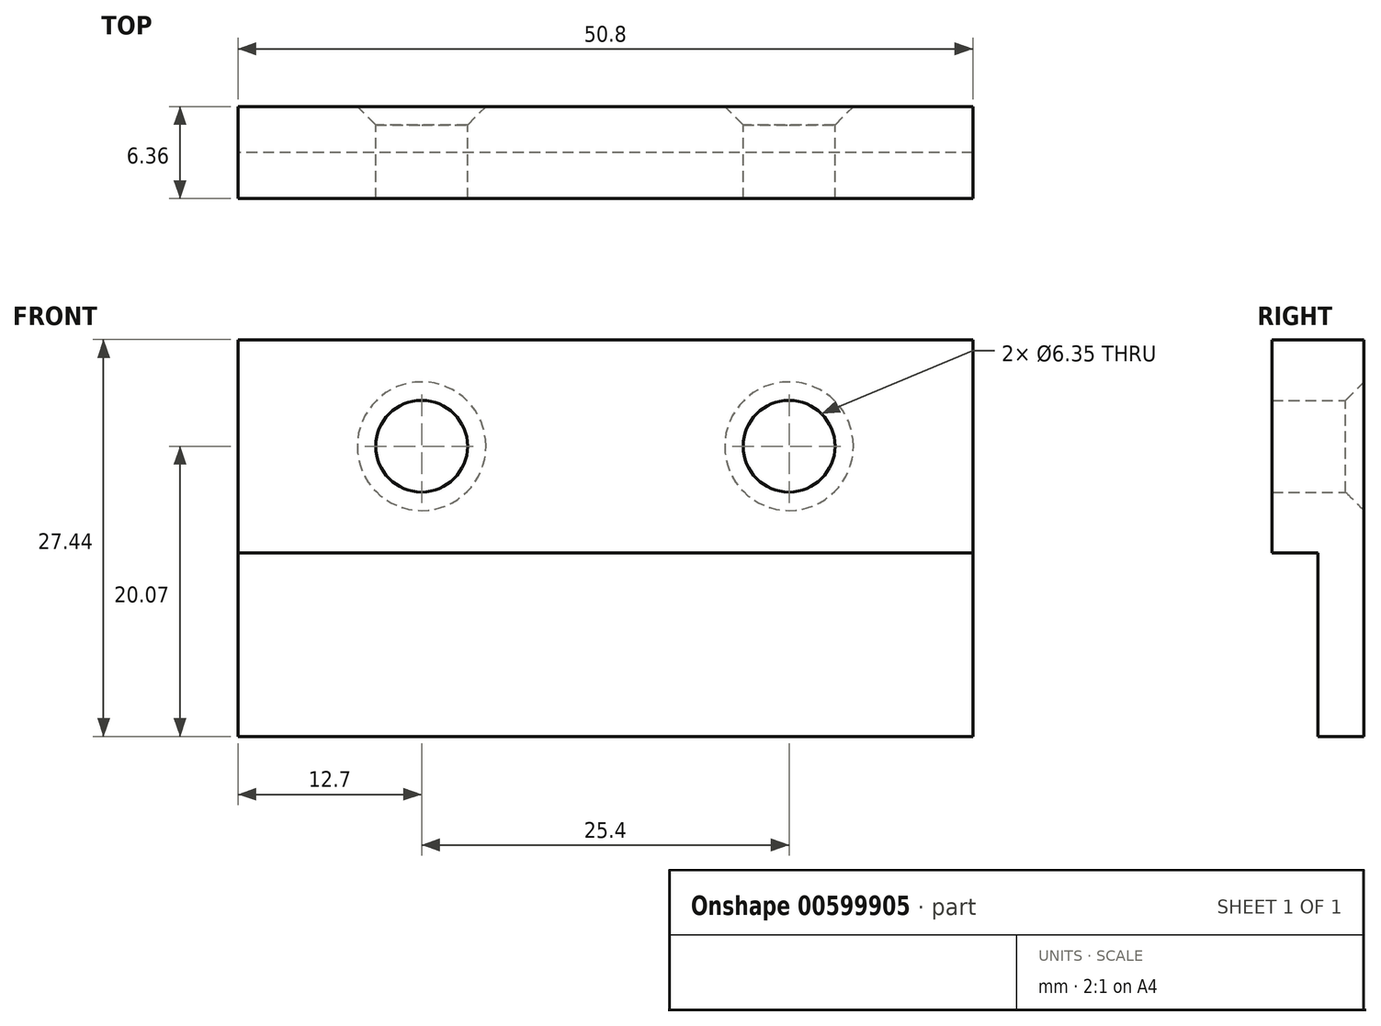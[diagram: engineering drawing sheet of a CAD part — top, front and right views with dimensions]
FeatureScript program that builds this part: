
annotation { "Feature Type Name" : "Feature", "Feature Type Description" : "" }
export const myFeature = defineFeature(function(context is Context, id is Id, definition is map)
    precondition{}
    {
        {
            var Q0;
            Q0=qCreatedBy(makeId("Front.planeOp"),FACE);
            var sketch = newSketch(context, id + "F0", { "sketchPlane" : qUnion([Q0])});
            skLineSegment(sketch, "E0.bottom", {"start": v(25.4, -7.37) * mm, "end": v(-25.4, -7.37) * mm});
            skLineSegment(sketch, "E0.top", {"start": v(25.4, 7.37) * mm, "end": v(-25.4, 7.37) * mm});
            skLineSegment(sketch, "E0.left", {"start": v(25.4, -7.37) * mm, "end": v(25.4, 7.37) * mm});
            skLineSegment(sketch, "E0.right", {"start": v(-25.4, -7.37) * mm, "end": v(-25.4, 7.37) * mm});
            skPoint(sketch, "E0.middle", {"position": v(0, 0) * mm});
            skCircle(sketch, "E1", {"center": v(12.7, 0) * mm, "radius": 3.18 * mm});
            skCircle(sketch, "E2", {"center": v(-12.7, 0) * mm, "radius": 3.18 * mm});
            skLineSegment(sketch, "E3", {"start": v(25.4, -7.37) * mm, "end": v(25.4, -20.07) * mm});
            skLineSegment(sketch, "E4", {"start": v(-25.4, -7.37) * mm, "end": v(-25.4, -20.07) * mm});
            skLineSegment(sketch, "E5", {"start": v(25.4, -20.07) * mm, "end": v(-25.4, -20.07) * mm});
            skSolve(sketch);
        }
        {
            var Q0;
            Q0=makeQuery(id+"F0.imprint","IMPRINT",FACE,{"disambiguationData":[TD([[makeQuery(id+"F0.imprint","IMPRINT",EDGE,{"derivedFrom":sQuery(id+"F0.wireOp",EDGE,"E0.bottom")}),-1.0]])]});
            extrude(context, id + "F1", {"entities" : qUnion([Q0]), "endBound" : BoundingType.SYMMETRIC, "depth" : 6.35 * mm, "offsetDistance" : 25.4 * mm});
        }
        {
            var Q0;
            Q0=makeQuery(id+"F0.imprint","IMPRINT",FACE,{"disambiguationData":[TD([[makeQuery(id+"F0.imprint","IMPRINT",EDGE,{"derivedFrom":sQuery(id+"F0.wireOp",EDGE,"E0.bottom")}),1.0]])]});
            extrude(context, id + "F2", {"entities" : qUnion([Q0]), "operationType" : NewBodyOperationType.ADD, "oppositeDirection" : true, "depth" : 3.17 * mm, "hasOffset" : true, "offsetDistance" : 4.83 * mm});
        }
        {
            var Q0;
            Q0=makeQuery(id+"F1.opExtrude","CAP_EDGE",EDGE,{"disambiguationData":[OSD([sQuery(id+"F0.wireOp",EDGE,"E1")])],"isStart":true});
            chamfer(context, id + "F3", {"entities" : qUnion([Q0]), "chamferType" : ChamferType.OFFSET_ANGLE, "width" : 1.27 * mm, "oppositeDirection" : false, "angle" : 45 * degree, "tangentPropagation" : true});
        }
        {
            var Q0;
            Q0=makeQuery(id+"F1.opExtrude","CAP_EDGE",EDGE,{"disambiguationData":[OSD([sQuery(id+"F0.wireOp",EDGE,"E2")])],"isStart":true});
            chamfer(context, id + "F4", {"entities" : qUnion([Q0]), "chamferType" : ChamferType.OFFSET_ANGLE, "width" : 1.27 * mm, "oppositeDirection" : false, "angle" : 45 * degree, "tangentPropagation" : true});
        }
    });
